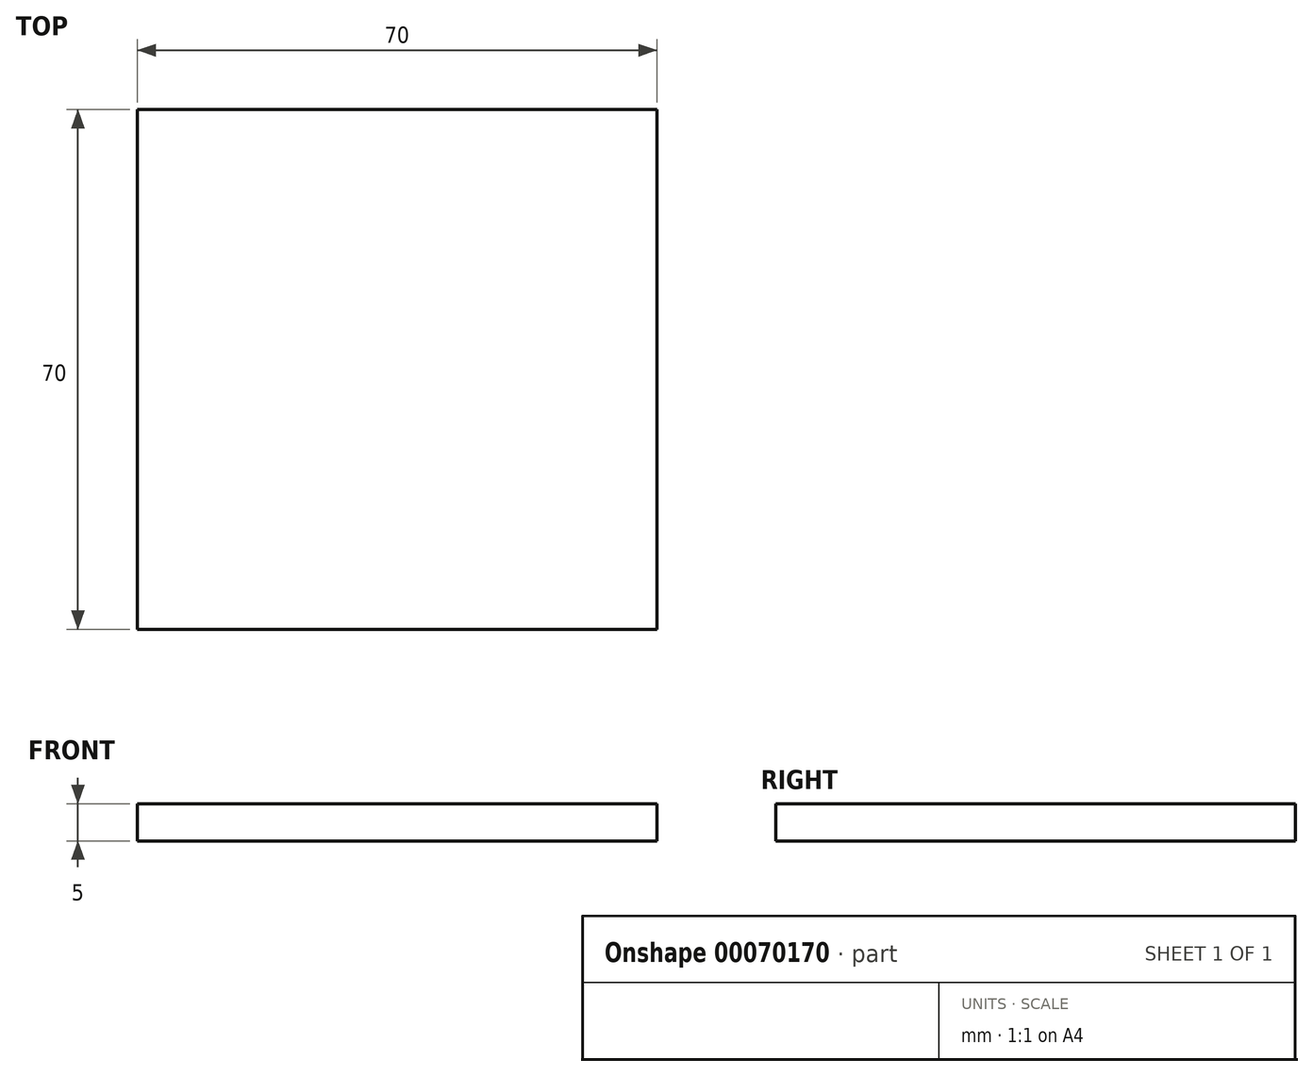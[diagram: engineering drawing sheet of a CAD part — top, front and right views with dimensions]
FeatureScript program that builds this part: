
annotation { "Feature Type Name" : "Feature", "Feature Type Description" : "" }
export const myFeature = defineFeature(function(context is Context, id is Id, definition is map)
    precondition{}
    {
        {
            var Q0;
            Q0=qCreatedBy(makeId("Top.planeOp"),FACE);
            var sketch = newSketch(context, id + "F0", { "sketchPlane" : qUnion([Q0])});
            skLineSegment(sketch, "E0.bottom", {"start": v(-21.07, 43.3) * mm, "end": v(48.93, 43.3) * mm});
            skLineSegment(sketch, "E0.top", {"start": v(-21.07, -26.7) * mm, "end": v(48.93, -26.7) * mm});
            skLineSegment(sketch, "E0.left", {"start": v(-21.07, 43.3) * mm, "end": v(-21.07, -26.7) * mm});
            skLineSegment(sketch, "E0.right", {"start": v(48.93, 43.3) * mm, "end": v(48.93, -26.7) * mm});
            skSolve(sketch);
        }
        {
            var Q0;
            Q0=makeQuery(id+"F0.imprint","IMPRINT",FACE,{"disambiguationData":[TD([[makeQuery(id+"F0.imprint","IMPRINT",EDGE,{"derivedFrom":sQuery(id+"F0.wireOp",EDGE,"E0.bottom")}),-1.0]])]});
            extrude(context, id + "F1", {"entities" : qUnion([Q0]), "depth" : 5 * mm});
        }
    });
